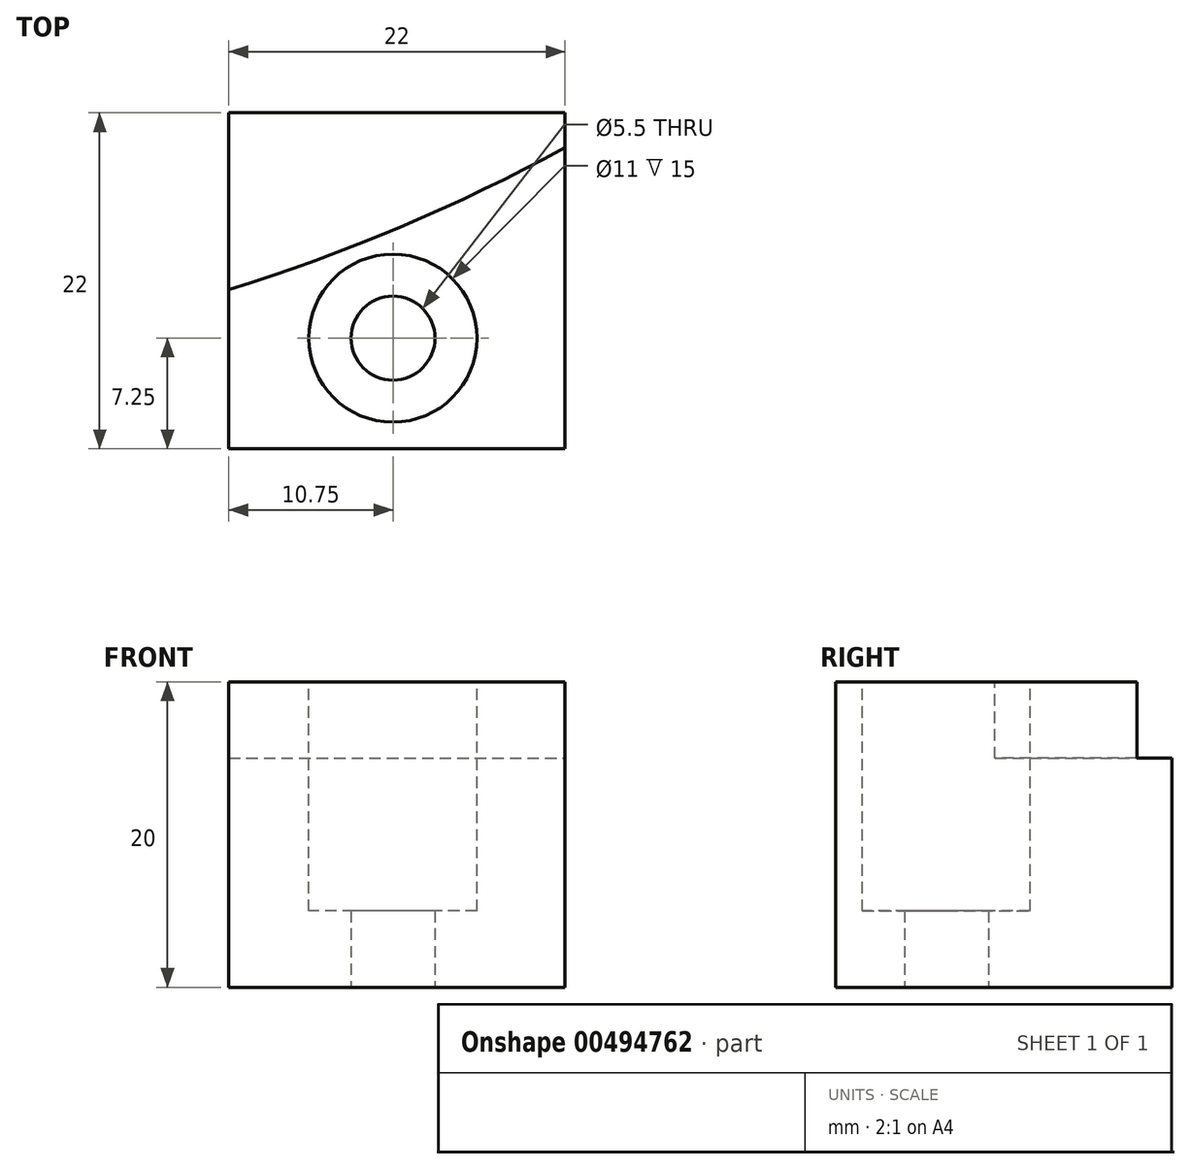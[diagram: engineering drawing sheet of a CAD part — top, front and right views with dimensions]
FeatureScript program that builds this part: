
annotation { "Feature Type Name" : "Feature", "Feature Type Description" : "" }
export const myFeature = defineFeature(function(context is Context, id is Id, definition is map)
    precondition{}
    {
        {
            var Q0;
            Q0=qCreatedBy(makeId("Top.planeOp"),FACE);
            var sketch = newSketch(context, id + "F0", { "sketchPlane" : qUnion([Q0])});
            skLineSegment(sketch, "E0.bottom", {"start": v(-22, 0) * mm, "end": v(0, 0) * mm});
            skLineSegment(sketch, "E0.top", {"start": v(-22, -22) * mm, "end": v(0, -22) * mm});
            skLineSegment(sketch, "E0.left", {"start": v(-22, 0) * mm, "end": v(-22, -22) * mm});
            skLineSegment(sketch, "E0.right", {"start": v(0, 0) * mm, "end": v(0, -22) * mm});
            skCircle(sketch, "E1", {"center": v(-11.25, -14.75) * mm, "radius": 2.75 * mm});
            skSolve(sketch);
        }
        {
            var Q0;
            Q0 = qSketchRegion(id + "F0", true);
            extrude(context, id + "F1", {"entities" : qUnion([Q0]), "depth" : 20 * mm});
        }
        {
            var Q0;
            Q0=makeQuery(id+"F1.opExtrude","CAP_FACE",FACE,{"disambiguationData":[OSD([sQuery(id+"F0.wireOp",EDGE,"E0.bottom"),sQuery(id+"F0.wireOp",EDGE,"E0.top"),sQuery(id+"F0.wireOp",EDGE,"E0.left"),sQuery(id+"F0.wireOp",EDGE,"E0.right"),sQuery(id+"F0.wireOp",EDGE,"E1")])],"isStart":false});
            var sketch = newSketch(context, id + "F2", { "sketchPlane" : qUnion([Q0])});
            skCircle(sketch, "E2.0", {"center": v(-11.25, -14.75) * mm, "radius": 2.75 * mm});
            skCircle(sketch, "E3.0", {"center": v(-11.25, -14.75) * mm, "radius": 5.5 * mm});
            skSolve(sketch);
        }
        {
            var Q0;
            Q0 = qSketchRegion(id + "F2", true);
            extrude(context, id + "F3", {"entities" : qUnion([Q0]), "operationType" : NewBodyOperationType.REMOVE, "oppositeDirection" : true, "depth" : 15 * mm});
        }
        {
            var Q0;
            Q0=makeQuery(id+"F1.opExtrude","CAP_FACE",FACE,{"disambiguationData":[OSD([sQuery(id+"F0.wireOp",EDGE,"E0.bottom"),sQuery(id+"F0.wireOp",EDGE,"E0.top"),sQuery(id+"F0.wireOp",EDGE,"E0.left"),sQuery(id+"F0.wireOp",EDGE,"E0.right"),sQuery(id+"F0.wireOp",EDGE,"E1")])],"isStart":false});
            var sketch = newSketch(context, id + "F4", { "sketchPlane" : qUnion([Q0])});
            skLineSegment(sketch, "E4.0.0", {"start": v(-22, 0) * mm, "end": v(-22, -22) * mm});
            skLineSegment(sketch, "E4.0.1", {"start": v(-22, -22) * mm, "end": v(0, -22) * mm});
            skLineSegment(sketch, "E4.0.2", {"start": v(0, -22) * mm, "end": v(0, 0) * mm});
            skLineSegment(sketch, "E4.0.3", {"start": v(0, 0) * mm, "end": v(-22, 0) * mm});
            skCircle(sketch, "E5", {"center": v(-57.43, 103.08) * mm, "radius": 120 * mm});
            skSolve(sketch);
        }
        {
            var Q0;
            {var subQ0=sQuery(id+"F4.wireOp",EDGE,"E4.0.3");Q0=makeQuery(id+"F4.imprint","IMPRINT",FACE,{"disambiguationData":[TD([[makeQuery(id+"F4.imprint","IMPRINT",EDGE,{"derivedFrom":subQ0}),-1.0]])]});}
            extrude(context, id + "F5", {"entities" : qUnion([Q0]), "operationType" : NewBodyOperationType.REMOVE, "oppositeDirection" : true, "depth" : 5 * mm});
        }
    });
